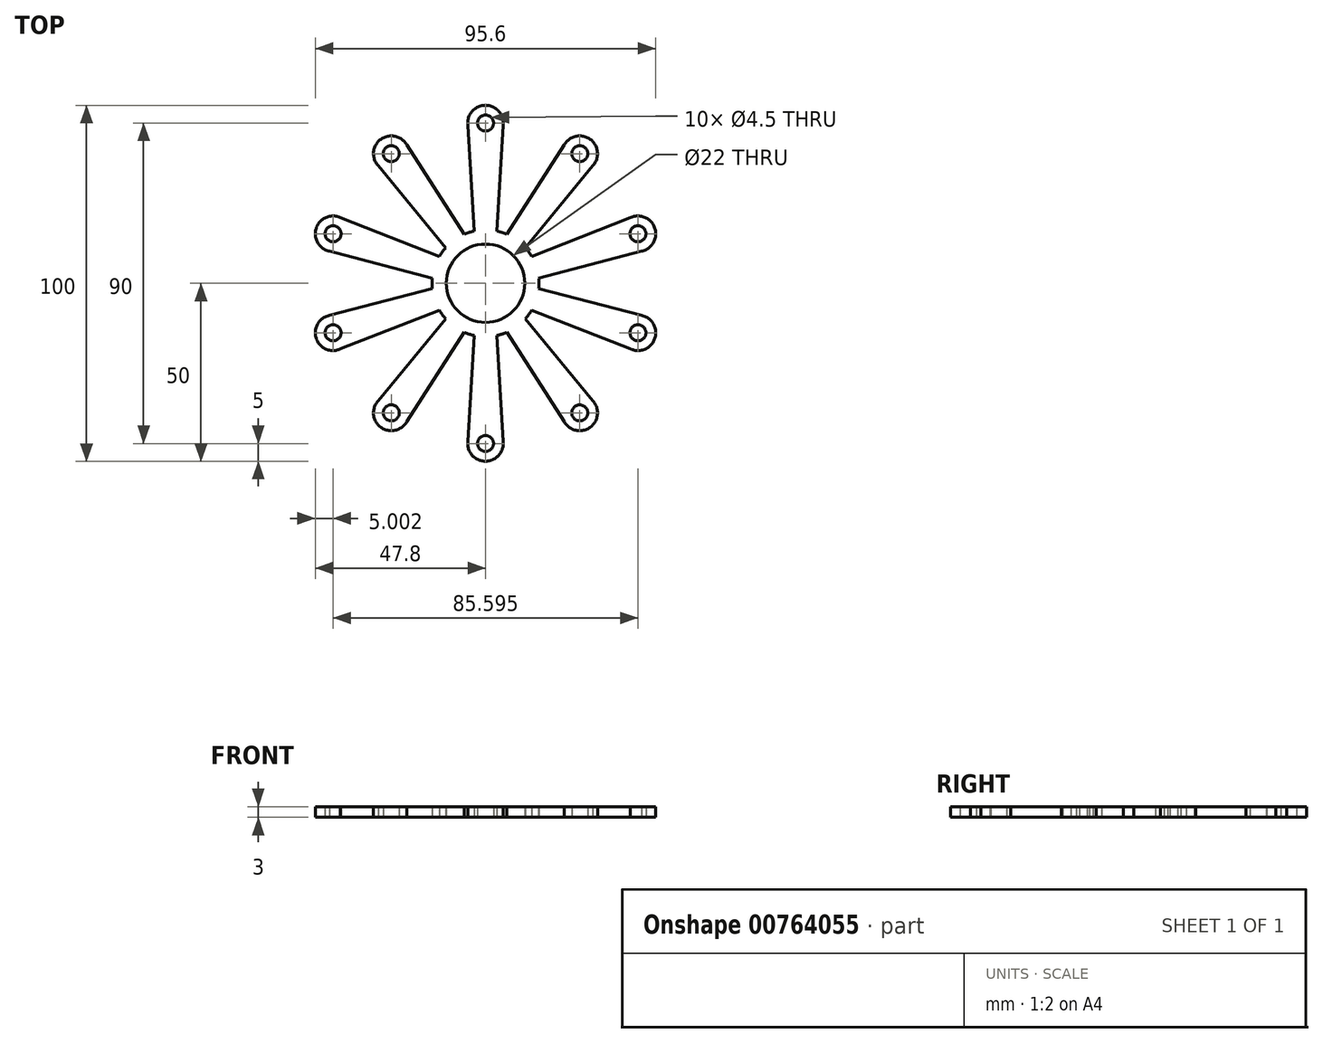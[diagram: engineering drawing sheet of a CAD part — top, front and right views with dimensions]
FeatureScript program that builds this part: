
annotation { "Feature Type Name" : "Feature", "Feature Type Description" : "" }
export const myFeature = defineFeature(function(context is Context, id is Id, definition is map)
    precondition{}
    {
        {
            var Q0;
            Q0=qCreatedBy(makeId("Top.planeOp"),FACE);
            var sketch = newSketch(context, id + "F0", { "sketchPlane" : qUnion([Q0])});
            skArc(sketch, "E0", {"start": v(3.4, 10.46) * mm, "mid": v(0, 11) * mm, "end": v(-3.4, 10.46) * mm});
            skArc(sketch, "E1", {"start": v(-3.21, 14.65) * mm, "mid": v(-3.93, 14.48) * mm, "end": v(-4.64, 14.27) * mm});
            skLineSegment(sketch, "E2", {"start": v(0, 42.75) * mm, "end": v(0, 45) * mm});
            skCircle(sketch, "E3", {"center": v(0, 45) * mm, "radius": 2.25 * mm});
            skArc(sketch, "E4", {"start": v(4.97, 44.41) * mm, "mid": v(0, 50) * mm, "end": v(-4.97, 44.41) * mm});
            skLineSegment(sketch, "E5", {"start": v(-5, 45) * mm, "end": v(-3.21, 14.65) * mm});
            skLineSegment(sketch, "E6", {"start": v(5, 45) * mm, "end": v(3.21, 14.65) * mm});
            skArc(sketch, "E7.trimOffspring", {"start": v(4.64, 14.27) * mm, "mid": v(3.93, 14.48) * mm, "end": v(3.21, 14.65) * mm});
            skCircle(sketch, "E8.1.0", {"center": v(-26.45, 36.4) * mm, "radius": 2.25 * mm});
            skArc(sketch, "E8.1.1", {"start": v(-22.09, 38.85) * mm, "mid": v(-29.39, 40.45) * mm, "end": v(-30.12, 33.01) * mm});
            skLineSegment(sketch, "E8.1.2", {"start": v(-22.4, 39.34) * mm, "end": v(-6.01, 13.74) * mm});
            skArc(sketch, "E8.1.3", {"start": v(-4.64, 14.27) * mm, "mid": v(-5.33, 14.02) * mm, "end": v(-6.01, 13.74) * mm});
            skArc(sketch, "E8.1.4", {"start": v(-11.21, 9.97) * mm, "mid": v(-11.69, 9.4) * mm, "end": v(-12.14, 8.82) * mm});
            skArc(sketch, "E8.1.5", {"start": v(-3.4, 10.46) * mm, "mid": v(-6.47, 8.9) * mm, "end": v(-8.9, 6.47) * mm});
            skLineSegment(sketch, "E8.1.6", {"start": v(-30.5, 33.47) * mm, "end": v(-11.21, 9.97) * mm});
            skCircle(sketch, "E8.2.0", {"center": v(-42.8, 13.9) * mm, "radius": 2.25 * mm});
            skArc(sketch, "E8.2.1", {"start": v(-40.7, 18.45) * mm, "mid": v(-47.55, 15.45) * mm, "end": v(-43.77, 9) * mm});
            skLineSegment(sketch, "E8.2.2", {"start": v(-41.25, 18.66) * mm, "end": v(-12.94, 7.58) * mm});
            skArc(sketch, "E8.2.3", {"start": v(-12.14, 8.82) * mm, "mid": v(-12.55, 8.2) * mm, "end": v(-12.94, 7.58) * mm});
            skArc(sketch, "E8.2.4", {"start": v(-14.93, 1.47) * mm, "mid": v(-14.98, 0.74) * mm, "end": v(-15, 0) * mm});
            skArc(sketch, "E8.2.5", {"start": v(-8.9, 6.47) * mm, "mid": v(-10.46, 3.4) * mm, "end": v(-11, 0) * mm});
            skLineSegment(sketch, "E8.2.6", {"start": v(-44.34, 9.15) * mm, "end": v(-14.93, 1.47) * mm});
            skCircle(sketch, "E8.3.0", {"center": v(-42.8, -13.9) * mm, "radius": 2.25 * mm});
            skArc(sketch, "E8.3.1", {"start": v(-43.77, -9) * mm, "mid": v(-47.55, -15.45) * mm, "end": v(-40.7, -18.45) * mm});
            skLineSegment(sketch, "E8.3.2", {"start": v(-44.34, -9.15) * mm, "end": v(-14.93, -1.47) * mm});
            skArc(sketch, "E8.3.3", {"start": v(-15, 0) * mm, "mid": v(-14.98, -0.74) * mm, "end": v(-14.93, -1.47) * mm});
            skArc(sketch, "E8.3.4", {"start": v(-12.94, -7.58) * mm, "mid": v(-12.55, -8.2) * mm, "end": v(-12.14, -8.82) * mm});
            skArc(sketch, "E8.3.5", {"start": v(-11, 0) * mm, "mid": v(-10.46, -3.4) * mm, "end": v(-8.9, -6.47) * mm});
            skLineSegment(sketch, "E8.3.6", {"start": v(-41.25, -18.66) * mm, "end": v(-12.94, -7.58) * mm});
            skCircle(sketch, "E8.4.0", {"center": v(-26.45, -36.4) * mm, "radius": 2.25 * mm});
            skArc(sketch, "E8.4.1", {"start": v(-30.12, -33.01) * mm, "mid": v(-29.39, -40.45) * mm, "end": v(-22.09, -38.85) * mm});
            skLineSegment(sketch, "E8.4.2", {"start": v(-30.5, -33.47) * mm, "end": v(-11.21, -9.97) * mm});
            skArc(sketch, "E8.4.3", {"start": v(-12.14, -8.82) * mm, "mid": v(-11.69, -9.4) * mm, "end": v(-11.21, -9.97) * mm});
            skArc(sketch, "E8.4.4", {"start": v(-6.01, -13.74) * mm, "mid": v(-5.33, -14.02) * mm, "end": v(-4.64, -14.27) * mm});
            skArc(sketch, "E8.4.5", {"start": v(-8.9, -6.47) * mm, "mid": v(-6.47, -8.9) * mm, "end": v(-3.4, -10.46) * mm});
            skLineSegment(sketch, "E8.4.6", {"start": v(-22.4, -39.34) * mm, "end": v(-6.01, -13.74) * mm});
            skCircle(sketch, "E8.5.0", {"center": v(0, -45) * mm, "radius": 2.25 * mm});
            skArc(sketch, "E8.5.1", {"start": v(-4.97, -44.41) * mm, "mid": v(0, -50) * mm, "end": v(4.97, -44.41) * mm});
            skLineSegment(sketch, "E8.5.2", {"start": v(-5, -45) * mm, "end": v(-3.21, -14.65) * mm});
            skArc(sketch, "E8.5.3", {"start": v(-4.64, -14.27) * mm, "mid": v(-3.93, -14.48) * mm, "end": v(-3.21, -14.65) * mm});
            skArc(sketch, "E8.5.4", {"start": v(3.21, -14.65) * mm, "mid": v(3.93, -14.48) * mm, "end": v(4.64, -14.27) * mm});
            skArc(sketch, "E8.5.5", {"start": v(-3.4, -10.46) * mm, "mid": v(0, -11) * mm, "end": v(3.4, -10.46) * mm});
            skLineSegment(sketch, "E8.5.6", {"start": v(5, -45) * mm, "end": v(3.21, -14.65) * mm});
            skCircle(sketch, "E8.6.0", {"center": v(26.45, -36.4) * mm, "radius": 2.25 * mm});
            skArc(sketch, "E8.6.1", {"start": v(22.09, -38.85) * mm, "mid": v(29.39, -40.45) * mm, "end": v(30.12, -33.01) * mm});
            skLineSegment(sketch, "E8.6.2", {"start": v(22.4, -39.34) * mm, "end": v(6.01, -13.74) * mm});
            skArc(sketch, "E8.6.3", {"start": v(4.64, -14.27) * mm, "mid": v(5.33, -14.02) * mm, "end": v(6.01, -13.74) * mm});
            skArc(sketch, "E8.6.4", {"start": v(11.21, -9.97) * mm, "mid": v(11.69, -9.4) * mm, "end": v(12.14, -8.82) * mm});
            skArc(sketch, "E8.6.5", {"start": v(3.4, -10.46) * mm, "mid": v(6.47, -8.9) * mm, "end": v(8.9, -6.47) * mm});
            skLineSegment(sketch, "E8.6.6", {"start": v(30.5, -33.47) * mm, "end": v(11.21, -9.97) * mm});
            skCircle(sketch, "E8.7.0", {"center": v(42.8, -13.9) * mm, "radius": 2.25 * mm});
            skArc(sketch, "E8.7.1", {"start": v(40.7, -18.45) * mm, "mid": v(47.55, -15.45) * mm, "end": v(43.77, -9) * mm});
            skLineSegment(sketch, "E8.7.2", {"start": v(41.25, -18.66) * mm, "end": v(12.94, -7.58) * mm});
            skArc(sketch, "E8.7.3", {"start": v(12.14, -8.82) * mm, "mid": v(12.55, -8.2) * mm, "end": v(12.94, -7.58) * mm});
            skArc(sketch, "E8.7.4", {"start": v(14.93, -1.47) * mm, "mid": v(14.98, -0.74) * mm, "end": v(15, 0) * mm});
            skArc(sketch, "E8.7.5", {"start": v(8.9, -6.47) * mm, "mid": v(10.46, -3.4) * mm, "end": v(11, 0) * mm});
            skLineSegment(sketch, "E8.7.6", {"start": v(44.34, -9.15) * mm, "end": v(14.93, -1.47) * mm});
            skCircle(sketch, "E8.8.0", {"center": v(42.8, 13.9) * mm, "radius": 2.25 * mm});
            skArc(sketch, "E8.8.1", {"start": v(43.77, 9) * mm, "mid": v(47.55, 15.45) * mm, "end": v(40.7, 18.45) * mm});
            skLineSegment(sketch, "E8.8.2", {"start": v(44.34, 9.15) * mm, "end": v(14.93, 1.47) * mm});
            skArc(sketch, "E8.8.3", {"start": v(15, 0) * mm, "mid": v(14.98, 0.74) * mm, "end": v(14.93, 1.47) * mm});
            skArc(sketch, "E8.8.4", {"start": v(12.94, 7.58) * mm, "mid": v(12.55, 8.2) * mm, "end": v(12.14, 8.82) * mm});
            skArc(sketch, "E8.8.5", {"start": v(11, 0) * mm, "mid": v(10.46, 3.4) * mm, "end": v(8.9, 6.47) * mm});
            skLineSegment(sketch, "E8.8.6", {"start": v(41.25, 18.66) * mm, "end": v(12.94, 7.58) * mm});
            skCircle(sketch, "E8.9.0", {"center": v(26.45, 36.4) * mm, "radius": 2.25 * mm});
            skArc(sketch, "E8.9.1", {"start": v(30.12, 33.01) * mm, "mid": v(29.39, 40.45) * mm, "end": v(22.09, 38.85) * mm});
            skLineSegment(sketch, "E8.9.2", {"start": v(30.5, 33.47) * mm, "end": v(11.21, 9.97) * mm});
            skArc(sketch, "E8.9.3", {"start": v(12.14, 8.82) * mm, "mid": v(11.69, 9.4) * mm, "end": v(11.21, 9.97) * mm});
            skArc(sketch, "E8.9.4", {"start": v(6.01, 13.74) * mm, "mid": v(5.33, 14.02) * mm, "end": v(4.64, 14.27) * mm});
            skArc(sketch, "E8.9.5", {"start": v(8.9, 6.47) * mm, "mid": v(6.47, 8.9) * mm, "end": v(3.4, 10.46) * mm});
            skLineSegment(sketch, "E8.9.6", {"start": v(22.4, 39.34) * mm, "end": v(6.01, 13.74) * mm});
            skPoint(sketch, "E9.orphan", {"position": v(0, 15) * mm});
            skSolve(sketch);
        }
        {
            var Q0;
            Q0 = qSketchRegion(id + "F0", true);
            extrude(context, id + "F1", {"entities" : qUnion([Q0]), "depth" : 3 * mm, "offsetDistance" : 25 * mm});
        }
    });
